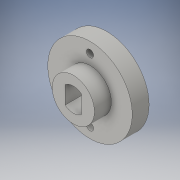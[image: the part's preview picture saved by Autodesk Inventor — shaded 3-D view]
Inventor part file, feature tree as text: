
AUTODESK INVENTOR PART (.ipt)
format: ipt  version: 2016 (Build 200138000, 138)  size: 129,024 bytes
history: native  units: in
note: dims shown in document units (in); Inventor stores cm internally (conversion verified against a paired STEP export)
features: extrude x2, sketch x2
ambient origin geometry x8: Origin, YZ Plane, XZ Plane, XY Plane, X Axis, Y Axis, Z Axis, Center Point
bodies: Solid1 (feature_tree)
feature tree (4):
  extrude  "Extrusion1"  Depth=0.2in
  extrude  "Extrusion2"  Depth=0.1533in
  sketch  "Sketch1"  dims[d14=0.2in d15=0.0in d16=1.0in]
  sketch  "Sketch2"  dims[d17=0.085in d18=0.085in d19=0.085in d20=0.2in d21=0.0in d26=0.5in d27=0.21in d28=0.195in d29=0.1533in d30=0.1533in d31=0.21in d32=0.11in d33=0.0133in d34=0.0975in d35=0.0975in]
